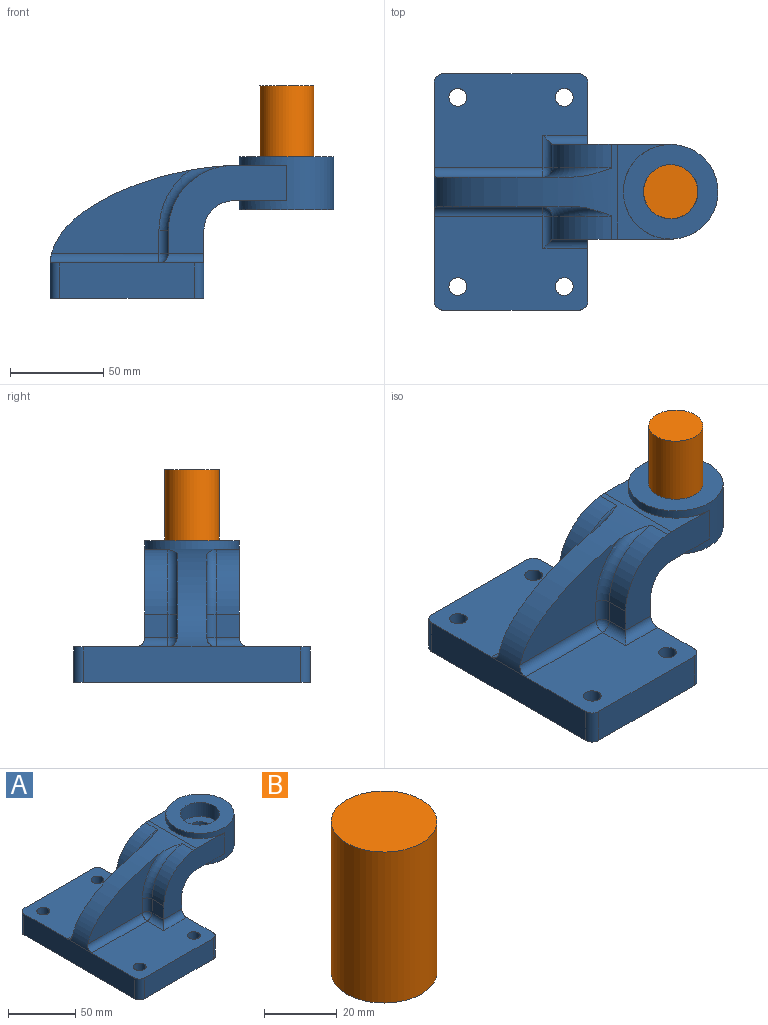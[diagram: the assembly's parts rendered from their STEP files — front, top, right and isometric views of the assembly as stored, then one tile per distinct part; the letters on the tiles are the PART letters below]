
ASSEMBLY  parts=2 mates=1
PART A: 45 faces, bbox 152.4x127x83.5 mm
  f0: cylinder r=7.94mm len=15.88mm, axis (0,0,1), area 791.7mm2, adj f21,f44
  f1: plane 12.4x12.38mm, normal (-1,0,0), area 153.5mm2, adj f3,f17,f33,f36
  f2: plane 82.55x50.48mm, normal (0,0,1), area 3592.4mm2, adj f5,f7,f9,f23,f24,f27,f28,f31
  f3: cylinder r=34.92mm len=34.77mm, axis (0,1,0), area 638.8mm2, adj f1,f10,f17,f35
  f4: plane 82.55x50.48mm, normal (0,0,1), area 3592.4mm2, adj f5,f7,f8,f25,f26,f29,f30,f37
  f5: plane 116.84x19.05mm, normal (-1,0,0), area 2225.8mm2, adj f2,f4,f6,f10,f24,f26
  f6: plane 127x82.55mm, normal (0,0,-1), area 10176.7mm2, adj f5,f7,f8,f9,f23,f24,f25,f26
  f7: plane 116.84x36.53mm, normal (1,0,0), area 3124.6mm2, adj f2,f4,f6,f13,f16,f17,f23,f25
  f8: plane 72.39x19.05mm, normal (0,-1,0), area 1379mm2, adj f4,f6,f25,f26
  f9: plane 72.39x19.05mm, normal (0,1,0), area 1379mm2, adj f2,f6,f23,f24
  f10: extruded ~98.43x52.4mm, area 2090.6mm2, adj f3,f5,f11,f15,f16,f17,f18,f19
  f11: cylinder r=34.92mm len=34.77mm, axis (0,1,0), area 638.8mm2, adj f10,f12,f16,f41
  f12: plane 12.4x12.38mm, normal (-1,0,0), area 153.5mm2, adj f11,f16,f38,f42
  f13: cylinder r=15.88mm len=50.8mm, axis (0,1,0), area 1266.8mm2, adj f7,f14,f16,f17
  f14: plane 50.8x28.58mm, normal (0,0,-1), area 438.2mm2, adj f13,f16,f17,f20
  f15: plane 50.8x28.58mm, normal (0,0,1), area 438.2mm2, adj f10,f16,f17,f20
  f16: plane 63.5x47.32mm, normal (0,-1,0), area 1540.5mm2, adj f7,f10,f11,f12,f13,f14,f15,f20
  f17: plane 63.5x47.32mm, normal (0,1,0), area 1540.5mm2, adj f1,f3,f7,f10,f13,f14,f15,f20
  f18: plane 77.87x50.44mm, normal (0,-1,0), area 1701.8mm2, adj f10,f39,f41,f42
  f19: plane 77.87x50.44mm, normal (0,1,0), area 1701.8mm2, adj f10,f32,f35,f36
  f20: cylinder r=25.4mm len=50.8mm, axis (0,0,-1), area 3040.2mm2, adj f14,f15,f16,f17,f21,f22
  f21: plane 50.8x50.8mm, normal (0,0,-1), area 1828.9mm2, adj f0,f20
  f22: plane 50.8x50.8mm, normal (0,0,1), area 1357mm2, adj f20,f43
  f23: cylinder r=5.08mm len=19.05mm, axis (0,0,1), area 152mm2, adj f2,f6,f7,f9
  f24: cylinder r=5.08mm len=19.05mm, axis (0,0,-1), area 152mm2, adj f2,f5,f6,f9
  f25: cylinder r=5.08mm len=19.05mm, axis (0,0,-1), area 152mm2, adj f4,f6,f7,f8
  f26: cylinder r=5.08mm len=19.05mm, axis (0,0,1), area 152mm2, adj f4,f5,f6,f8
  f27: cylinder r=4.76mm len=19.05mm, axis (0,0,1), area 570mm2, adj f2,f6
  f28: cylinder r=4.76mm len=19.05mm, axis (0,0,1), area 570mm2, adj f2,f6
  f29: cylinder r=4.76mm len=19.05mm, axis (0,0,1), area 570mm2, adj f4,f6
  f30: cylinder r=4.76mm len=19.05mm, axis (0,0,1), area 570mm2, adj f4,f6
  f31: cylinder r=5.08mm len=24.13mm, axis (1,0,0), area 166.7mm2, adj f2,f7,f17,f33
  f32: cylinder r=5.08mm len=58.42mm, axis (1,0,0), area 464.4mm2, adj f2,f10,f19,f34
  f33: cylinder r=5.08mm len=17.46mm, axis (0,-1,0), area 113.5mm2, adj f1,f2,f31,f34
  f34: sphere r=5.08mm, area 40.5mm2, adj f32,f33,f36
  f35: torus R=40mm, axis (0,-1,0), area 350.5mm2, adj f3,f10,f19,f36
  f36: cylinder r=5.08mm len=12.4mm, axis (0,0,1), area 98.9mm2, adj f1,f19,f34,f35
  f37: cylinder r=5.08mm len=24.13mm, axis (-1,0,0), area 166.7mm2, adj f4,f7,f16,f38
  f38: cylinder r=5.08mm len=17.46mm, axis (0,-1,0), area 113.5mm2, adj f4,f12,f37,f40
  f39: cylinder r=5.08mm len=58.42mm, axis (-1,0,0), area 464.4mm2, adj f4,f10,f18,f40
  f40: sphere r=5.08mm, area 40.5mm2, adj f38,f39,f42
  f41: torus R=40mm, axis (0,-1,0), area 350.5mm2, adj f10,f11,f18,f42
  f42: cylinder r=5.08mm len=12.4mm, axis (0,0,-1), area 98.9mm2, adj f12,f18,f40,f41
  f43: cylinder r=14.6mm len=29.2mm, axis (0,0,1), area 1165.2mm2, adj f22,f44
  f44: plane 29.2x29.2mm, normal (0,0,1), area 471.9mm2, adj f0,f43
PART B: 3 faces, bbox 29.1x29.1x50.8 mm
  f0: cylinder r=14.54mm len=50.8mm, axis (0,0,-1), area 4640.5mm2, adj f1,f2
  f1: plane 29.08x29.08mm, normal (0,0,1), area 664mm2, adj f0
  f2: plane 29.08x29.08mm, normal (0,0,-1), area 664mm2, adj f0
PLACE A t=(-88.79,7.44,10.18)mm fixed
PLACE B t=(-88.79,7.44,10.18)mm
MATE fastened A.f0 <-> B.f0  axis (0,0,1) through (-3.06,7.44,64.16)mm
